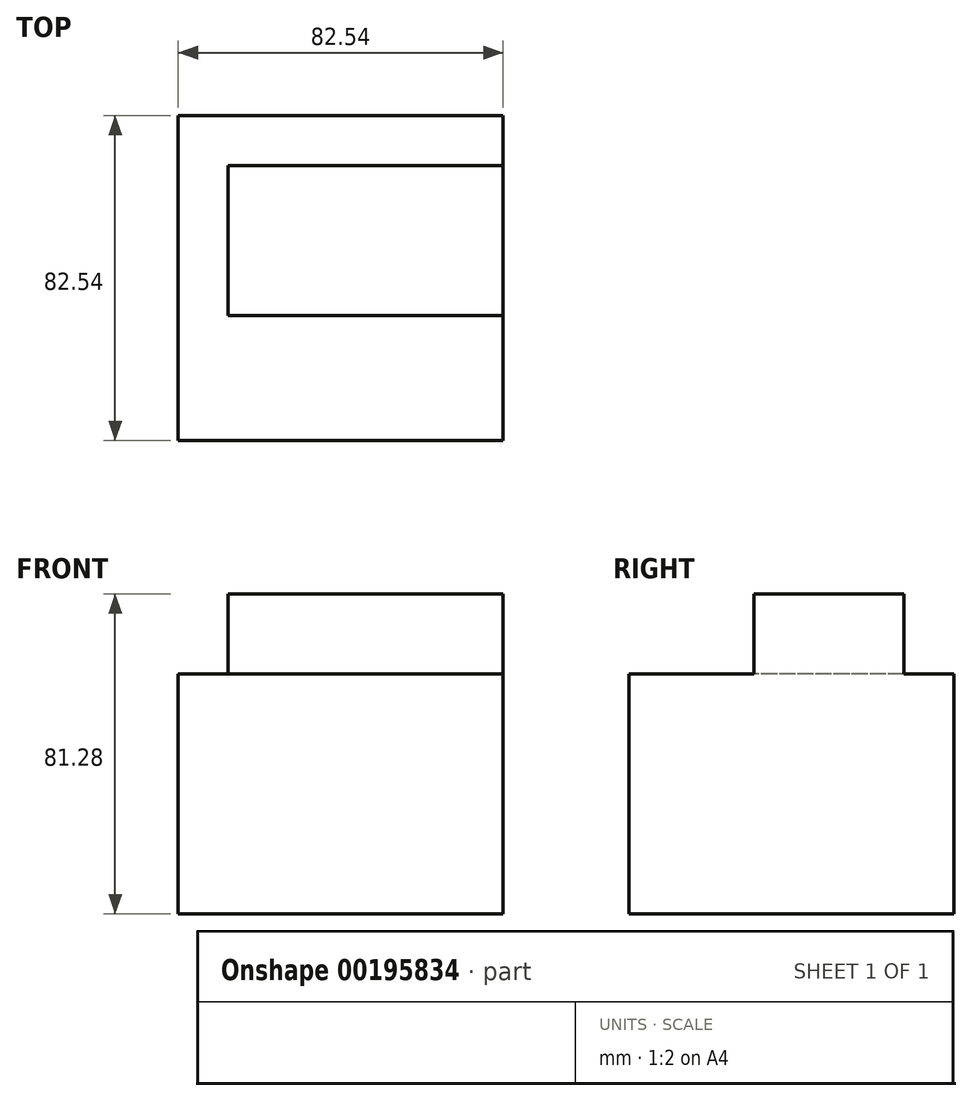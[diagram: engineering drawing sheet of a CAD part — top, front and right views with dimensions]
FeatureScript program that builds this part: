
annotation { "Feature Type Name" : "Feature", "Feature Type Description" : "" }
export const myFeature = defineFeature(function(context is Context, id is Id, definition is map)
    precondition{}
    {
        {
            var Q0;
            Q0=qCreatedBy(makeId("Top.planeOp"),FACE);
            var sketch = newSketch(context, id + "F0", { "sketchPlane" : qUnion([Q0])});
            skLineSegment(sketch, "E0.bottom", {"start": v(-41.27, 41.28) * mm, "end": v(41.28, 41.28) * mm});
            skLineSegment(sketch, "E0.top", {"start": v(-41.28, -41.28) * mm, "end": v(41.27, -41.28) * mm});
            skLineSegment(sketch, "E0.left", {"start": v(-41.27, 41.28) * mm, "end": v(-41.28, -41.27) * mm});
            skLineSegment(sketch, "E0.right", {"start": v(41.28, 41.28) * mm, "end": v(41.27, -41.27) * mm});
            skPoint(sketch, "E0.middle", {"position": v(0, 0) * mm});
            skSolve(sketch);
        }
        {
            var Q0;
            Q0=makeQuery(id+"F0.imprint","IMPRINT",FACE,{"disambiguationData":[TD([[makeQuery(id+"F0.imprint","IMPRINT",EDGE,{"derivedFrom":sQuery(id+"F0.wireOp",EDGE,"E0.bottom")}),-1.0]])]});
            extrude(context, id + "F1", {"entities" : qUnion([Q0]), "depth" : 60.96 * mm});
        }
        {
            var Q0;
            Q0=qCreatedBy(makeId("Top.planeOp"),FACE);
            cPlane(context, id + "F2", {"entities" : qUnion([Q0]), "cplaneType" : CPlaneType.OFFSET, "offset" : 60.96 * mm, "width" : 152.4 * mm, "height" : 152.4 * mm});
        }
        {
            var Q0;
            Q0=qCreatedBy(id+"F2.planeOp",FACE);
            var sketch = newSketch(context, id + "F3", { "sketchPlane" : qUnion([Q0])});
            skLineSegment(sketch, "E1.bottom", {"start": v(-28.57, 28.58) * mm, "end": v(41.28, 28.58) * mm});
            skLineSegment(sketch, "E1.top", {"start": v(-28.58, -9.52) * mm, "end": v(41.28, -9.52) * mm});
            skLineSegment(sketch, "E1.left", {"start": v(-28.57, 28.58) * mm, "end": v(-28.57, -9.52) * mm});
            skLineSegment(sketch, "E1.right", {"start": v(41.28, 28.58) * mm, "end": v(41.28, -9.52) * mm});
            skPoint(sketch, "E1.middle", {"position": v(6.35, 9.53) * mm});
            skSolve(sketch);
        }
        {
            var Q0;
            Q0=makeQuery(id+"F3.imprint","IMPRINT",FACE,{"disambiguationData":[TD([[makeQuery(id+"F3.imprint","IMPRINT",EDGE,{"derivedFrom":sQuery(id+"F3.wireOp",EDGE,"E1.bottom")}),-1.0]])]});
            extrude(context, id + "F4", {"entities" : qUnion([Q0]), "operationType" : NewBodyOperationType.ADD, "depth" : 20.32 * mm});
        }
    });
